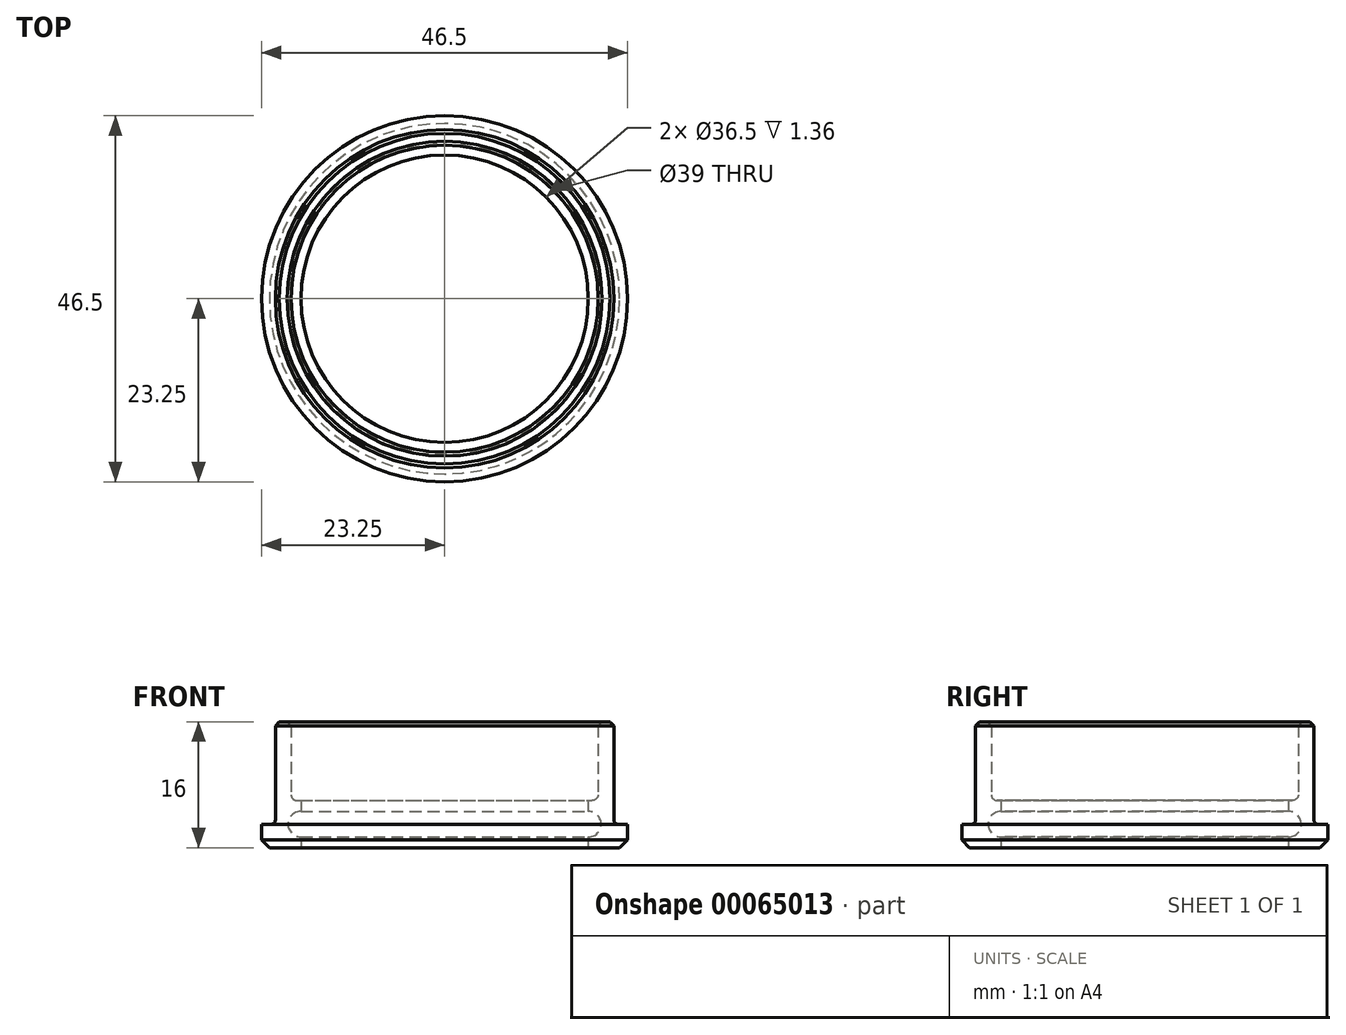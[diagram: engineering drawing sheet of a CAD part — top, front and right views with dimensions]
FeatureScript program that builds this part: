
annotation { "Feature Type Name" : "Feature", "Feature Type Description" : "" }
export const myFeature = defineFeature(function(context is Context, id is Id, definition is map)
    precondition{}
    {
        {
            var Q0;
            Q0=qCreatedBy(makeId("Right.planeOp"),FACE);
            var sketch = newSketch(context, id + "F0", { "sketchPlane" : qUnion([Q0])});
            skLineSegment(sketch, "E0.bottom", {"start": v(18.25, 3) * mm, "end": v(21.5, 3) * mm});
            skLineSegment(sketch, "E0.top", {"start": v(18.25, -3) * mm, "end": v(23.25, -3) * mm});
            skLineSegment(sketch, "E0.left", {"start": v(18.25, 3) * mm, "end": v(18.25, 1.64) * mm});
            skLineSegment(sketch, "E0.right", {"start": v(23.25, 0) * mm, "end": v(23.25, -3) * mm});
            skLineSegment(sketch, "E1", {"start": v(0, 0) * mm, "end": v(18.25, 0) * mm, "construction": true});
            skArc(sketch, "E2", {"start": v(18.25, -1.64) * mm, "mid": v(19.89, 0) * mm, "end": v(18.25, 1.64) * mm});
            skLineSegment(sketch, "E3.trimOffspring", {"start": v(18.25, -1.64) * mm, "end": v(18.25, -3) * mm});
            skLineSegment(sketch, "E4", {"start": v(0, 0) * mm, "end": v(0, 9.76) * mm, "construction": true});
            skLineSegment(sketch, "E5", {"start": v(21.5, 3) * mm, "end": v(21.5, 0) * mm});
            skLineSegment(sketch, "E6", {"start": v(21.5, 0) * mm, "end": v(23.25, 0) * mm});
            skLineSegment(sketch, "E7", {"start": v(21.5, 3) * mm, "end": v(21.5, 13) * mm});
            skLineSegment(sketch, "E8", {"start": v(21.5, 13) * mm, "end": v(19.5, 13) * mm});
            skLineSegment(sketch, "E9", {"start": v(19.5, 13) * mm, "end": v(19.5, 3) * mm});
            skLineSegment(sketch, "E10", {"start": v(15, 19) * mm, "end": v(15, 13) * mm});
            skLineSegment(sketch, "E11", {"start": v(15, 13) * mm, "end": v(19.5, 13) * mm});
            skLineSegment(sketch, "E12", {"start": v(15, 19) * mm, "end": v(13, 19) * mm});
            skLineSegment(sketch, "E13", {"start": v(13, 19) * mm, "end": v(13, 11) * mm});
            skLineSegment(sketch, "E14", {"start": v(13, 11) * mm, "end": v(19.5, 11) * mm});
            skSolve(sketch);
        }
        {
            var Q0;
            Q0=makeQuery(id+"F0.imprint","IMPRINT",FACE,{"disambiguationData":[TD([[makeQuery(id+"F0.imprint","IMPRINT",EDGE,{"derivedFrom":sQuery(id+"F0.wireOp",EDGE,"E0.bottom")}),-1.0]])]});
            var Q1;
            {var subQ1=sQuery(id+"F0.wireOp",EDGE,"E7");Q1=makeQuery(id+"F0.imprint","IMPRINT",FACE,{"disambiguationData":[TD([[makeQuery(id+"F0.imprint","IMPRINT",EDGE,{"derivedFrom":subQ1}),1.0]])]});}
            var Q2;
            Q2=sQuery(id+"F0.wireOp",EDGE,"E4");
            revolve(context, id + "F1", {"entities" : qUnion([Q0, Q1]), "axis" : qUnion([Q2]), "revolveType" : RevolveType.FULL});
        }
        {
            var Q0;
            Q0=makeQuery(id+"F1.opRevolve","SWEPT_EDGE",EDGE,{"disambiguationData":[OSD([sQuery(id+"F0.wireOp",EDGE,"E5"),sQuery(id+"F0.wireOp",EDGE,"E6")])]});
            fillet(context, id + "F2", {"entities" : qUnion([Q0]), "radius" : 0.5 * mm, "tangentPropagation" : true, "allowEdgeOverflow" : false});
        }
        {
            var Q0;
            Q0=makeQuery(id+"F1.opRevolve","SWEPT_EDGE",EDGE,{"disambiguationData":[OSD([sQuery(id+"F0.wireOp",EDGE,"E0.top"),sQuery(id+"F0.wireOp",EDGE,"E0.right")])]});
            chamfer(context, id + "F3", {"entities" : qUnion([Q0]), "width" : 1 * mm, "tangentPropagation" : true});
        }
        {
            var Q0;
            Q0=makeQuery(id+"F1.opRevolve","SWEPT_EDGE",EDGE,{"disambiguationData":[OSD([sQuery(id+"F0.wireOp",EDGE,"E7"),sQuery(id+"F0.wireOp",EDGE,"E8")])]});
            var Q1;
            Q1=makeQuery(id+"F1.opRevolve","SWEPT_EDGE",EDGE,{"disambiguationData":[OSD([sQuery(id+"F0.wireOp",EDGE,"E8"),sQuery(id+"F0.wireOp",EDGE,"E9"),sQuery(id+"F0.wireOp",EDGE,"E11")])]});
            chamfer(context, id + "F4", {"entities" : qUnion([Q0, Q1]), "width" : 0.5 * mm, "tangentPropagation" : true});
        }
        {
            var Q0;
            Q0=makeQuery(id+"F1.opRevolve","SWEPT_EDGE",EDGE,{"disambiguationData":[OSD([sQuery(id+"F0.wireOp",EDGE,"E0.bottom"),sQuery(id+"F0.wireOp",EDGE,"E9")])]});
            fillet(context, id + "F5", {"entities" : qUnion([Q0]), "radius" : 0.75 * mm, "tangentPropagation" : true, "allowEdgeOverflow" : false});
        }
    });
